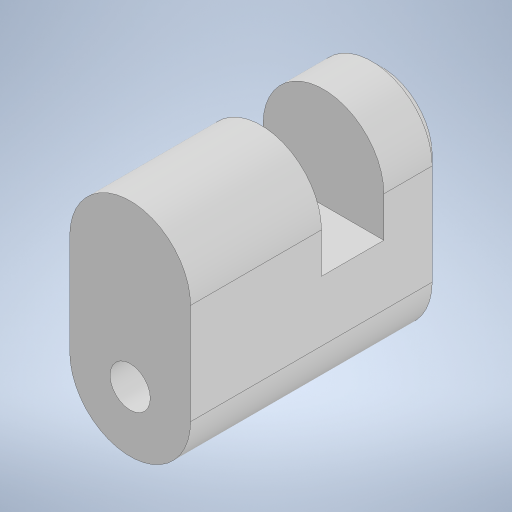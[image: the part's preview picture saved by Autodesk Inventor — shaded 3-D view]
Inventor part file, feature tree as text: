
AUTODESK INVENTOR PART (.ipt)
format: ipt  version: 2024.1 (Build 281209000, 209)  size: 237,056 bytes
history: native  units: mm
features: extrude x4, sketch x4, projected_geometry x3, chamfer x2
ambient origin geometry x8: Origin, YZ Plane, XZ Plane, XY Plane, X Axis, Y Axis, Z Axis, Center Point
bodies: Solid1 (feature_tree)
feature tree (13):
  extrude  "Extrusion1"  Depth=12.0mm
  extrude  "Extrusion2"  Depth=6.0mm
  extrude  "Extrusion3"  Depth=13.0mm TaperAngle=0.0deg
  extrude  "Extrusion4"  Depth=2.0mm TaperAngle=0.0deg
  chamfer  "Chamfer1"  Distance=2.0mm Angle=45.0deg
  chamfer  "Chamfer2"  Distance=2.0mm Angle=45.0deg
  sketch  "Sketch2"  dims[d0=12.0mm d1=4.0mm]
  sketch  "Sketch3"  dims[d2=25.0mm d3=0.0mm d4=6.0mm]
  projected_geometry  "Projected Loop1"
  sketch  "Sketch4"  dims[d5=10.0mm d6=13.0mm d7=0.0mm]
  projected_geometry  "Projected Loop2"
  sketch  "Sketch5"  dims[d8=5.8mm d9=0.0mm d10=6.4mm d11=0.0mm d12=3.0mm d13=2.0mm d14=45.0deg d15=1.0mm d16=2.0mm d17=45.0deg]
  projected_geometry  "Projected Loop3"
